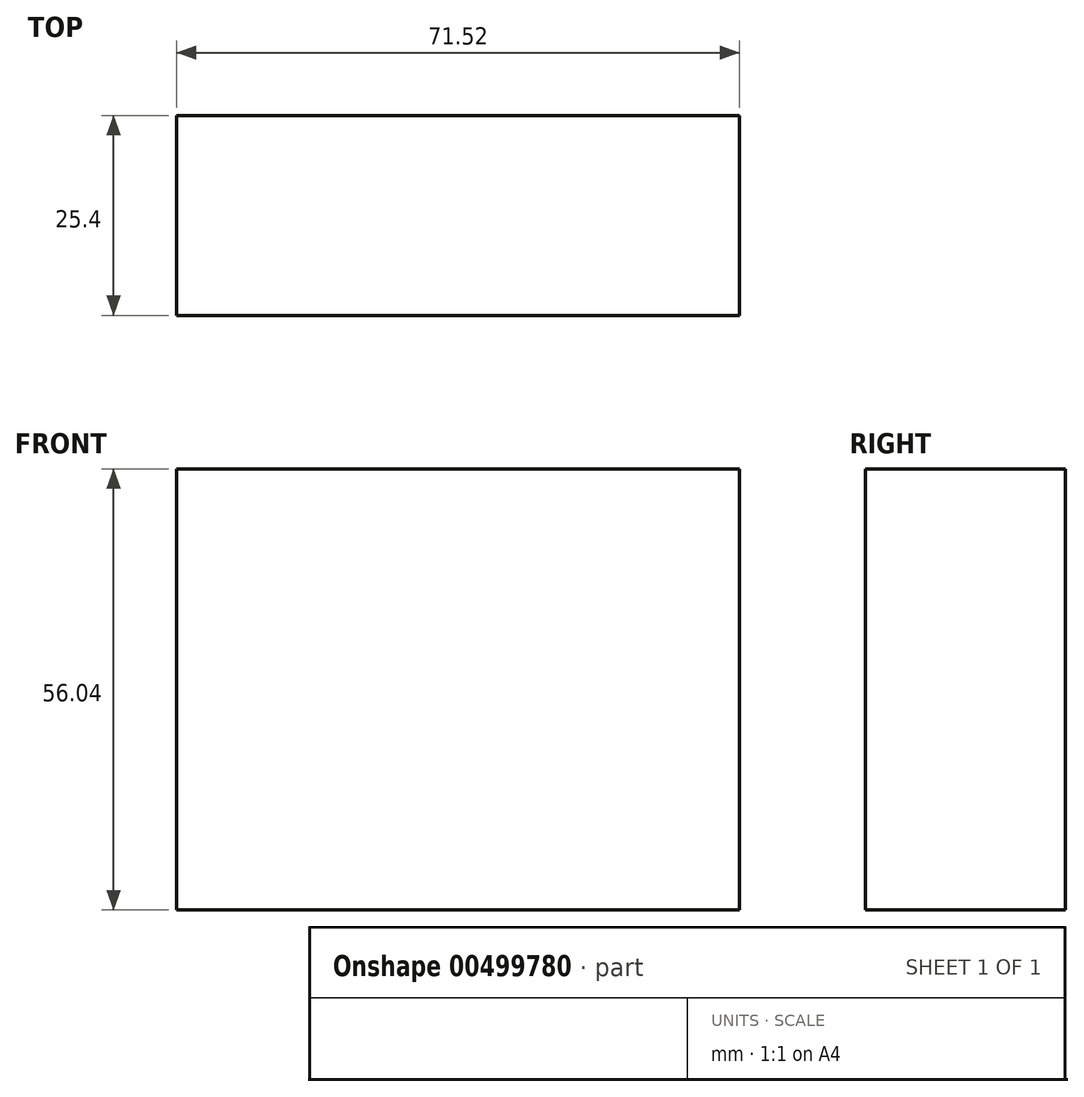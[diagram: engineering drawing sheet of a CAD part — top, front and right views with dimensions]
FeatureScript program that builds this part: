
annotation { "Feature Type Name" : "Feature", "Feature Type Description" : "" }
export const myFeature = defineFeature(function(context is Context, id is Id, definition is map)
    precondition{}
    {
        {
            var Q0;
            Q0=qCreatedBy(makeId("Front.planeOp"),FACE);
            var sketch = newSketch(context, id + "F0", { "sketchPlane" : qUnion([Q0])});
            skLineSegment(sketch, "E0.bottom", {"start": v(-35.76, 28.02) * mm, "end": v(35.76, 28.02) * mm});
            skLineSegment(sketch, "E0.top", {"start": v(-35.76, -28.02) * mm, "end": v(35.76, -28.02) * mm});
            skLineSegment(sketch, "E0.left", {"start": v(-35.76, 28.02) * mm, "end": v(-35.76, -28.02) * mm});
            skLineSegment(sketch, "E0.right", {"start": v(35.76, 28.02) * mm, "end": v(35.76, -28.02) * mm});
            skPoint(sketch, "E0.middle", {"position": v(0, 0) * mm});
            skSolve(sketch);
        }
        {
            var Q0;
            Q0 = qSketchRegion(id + "F0", true);
            extrude(context, id + "F1", {"entities" : qUnion([Q0]), "endBound" : BoundingType.SYMMETRIC, "depth" : 25.4 * mm});
        }
    });
